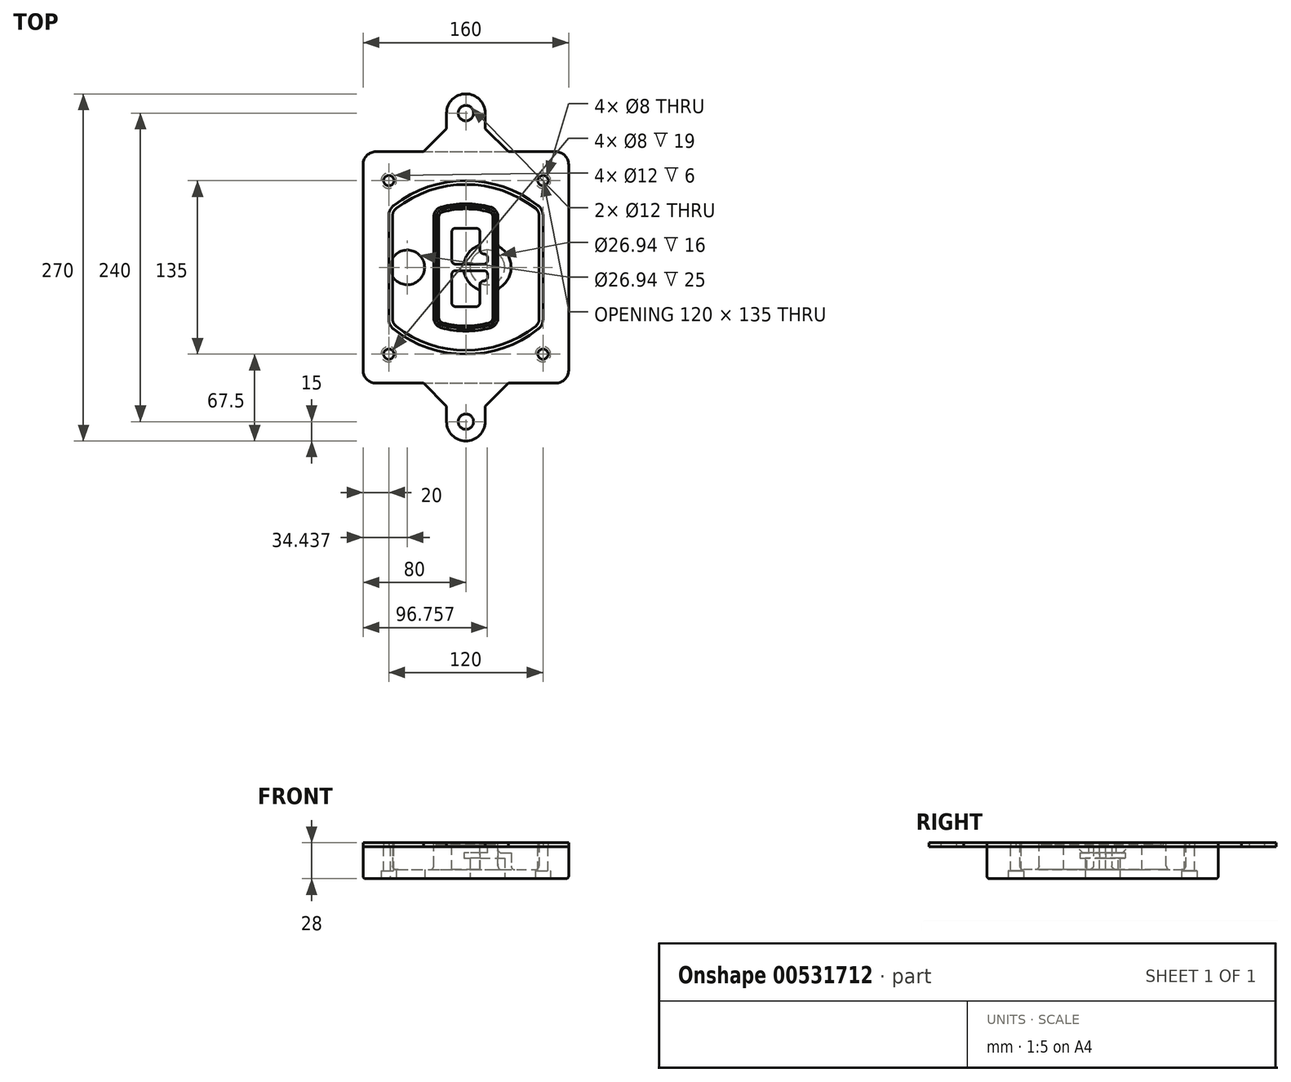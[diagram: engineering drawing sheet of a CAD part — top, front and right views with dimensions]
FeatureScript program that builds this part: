
annotation { "Feature Type Name" : "Feature", "Feature Type Description" : "" }
export const myFeature = defineFeature(function(context is Context, id is Id, definition is map)
    precondition{}
    {
        {
            var Q0;
            Q0=qCreatedBy(makeId("Top.planeOp"),FACE);
            var sketch = newSketch(context, id + "F0", { "sketchPlane" : qUnion([Q0])});
            skPoint(sketch, "E0.rect.middle", {"position": v(0, 0) * mm});
            skLineSegment(sketch, "E1.bottom", {"start": v(-70, -90) * mm, "end": v(70, -90) * mm});
            skLineSegment(sketch, "E1.top", {"start": v(-70, 90) * mm, "end": v(70, 90) * mm});
            skLineSegment(sketch, "E1.left", {"start": v(-80, -80) * mm, "end": v(-80, 80) * mm});
            skLineSegment(sketch, "E1.right", {"start": v(80, -80) * mm, "end": v(80, 80) * mm});
            skLineSegment(sketch, "E2", {"start": v(-80, 90) * mm, "end": v(80, -90) * mm, "construction": true});
            skLineSegment(sketch, "E3", {"start": v(80, 90) * mm, "end": v(-80, -90) * mm, "construction": true});
            skCircle(sketch, "E4", {"center": v(-60, 67.5) * mm, "radius": 4 * mm});
            skCircle(sketch, "E5", {"center": v(60, 67.5) * mm, "radius": 4 * mm});
            skCircle(sketch, "E6", {"center": v(60, -67.5) * mm, "radius": 4 * mm});
            skCircle(sketch, "E7", {"center": v(-60, -67.5) * mm, "radius": 4 * mm});
            skLineSegment(sketch, "E8", {"start": v(-60, 67.5) * mm, "end": v(60, 67.5) * mm, "construction": true});
            skLineSegment(sketch, "E9", {"start": v(60, 67.5) * mm, "end": v(60, -67.5) * mm, "construction": true});
            skLineSegment(sketch, "E10", {"start": v(60, -67.5) * mm, "end": v(-60, -67.5) * mm, "construction": true});
            skLineSegment(sketch, "E11", {"start": v(-60, -67.5) * mm, "end": v(-60, 67.5) * mm, "construction": true});
            skLineSegment(sketch, "E12", {"start": v(-60, 40.3) * mm, "end": v(-60, -40.3) * mm});
            skLineSegment(sketch, "E13", {"start": v(60, 40.3) * mm, "end": v(60, -40.3) * mm});
            skArc(sketch, "E14", {"start": v(56.15, 48.18) * mm, "mid": v(0, 67.5) * mm, "end": v(-56.15, 48.18) * mm});
            skArc(sketch, "E15", {"start": v(-56.15, -48.18) * mm, "mid": v(0, -67.5) * mm, "end": v(56.15, -48.18) * mm});
            skLineSegment(sketch, "E16", {"start": v(-60, 0) * mm, "end": v(60, 0) * mm, "construction": true});
            skPoint(sketch, "E17.visualSharp", {"position": v(-60, -45) * mm});
            skArc(sketch, "E17.filletArc", {"start": v(-60, -40.3) * mm, "mid": v(-58.99, -44.68) * mm, "end": v(-56.15, -48.18) * mm});
            skPoint(sketch, "E18.visualSharp", {"position": v(-60, 45) * mm});
            skArc(sketch, "E18.filletArc", {"start": v(-56.15, 48.18) * mm, "mid": v(-58.99, 44.68) * mm, "end": v(-60, 40.3) * mm});
            skPoint(sketch, "E19.visualSharp", {"position": v(60, 45) * mm});
            skArc(sketch, "E19.filletArc", {"start": v(60, 40.3) * mm, "mid": v(58.99, 44.68) * mm, "end": v(56.15, 48.18) * mm});
            skPoint(sketch, "E20.visualSharp", {"position": v(60, -45) * mm});
            skArc(sketch, "E20.filletArc", {"start": v(56.15, -48.18) * mm, "mid": v(58.99, -44.68) * mm, "end": v(60, -40.3) * mm});
            skPoint(sketch, "E21.visualSharp", {"position": v(-80, 90) * mm});
            skArc(sketch, "E21.filletArc", {"start": v(-70, 90) * mm, "mid": v(-77.07, 87.07) * mm, "end": v(-80, 80) * mm});
            skPoint(sketch, "E22.visualSharp", {"position": v(80, 90) * mm});
            skArc(sketch, "E22.filletArc", {"start": v(80, 80) * mm, "mid": v(77.07, 87.07) * mm, "end": v(70, 90) * mm});
            skPoint(sketch, "E23.visualSharp", {"position": v(80, -90) * mm});
            skArc(sketch, "E23.filletArc", {"start": v(70, -90) * mm, "mid": v(77.07, -87.07) * mm, "end": v(80, -80) * mm});
            skPoint(sketch, "E24.visualSharp", {"position": v(-80, -90) * mm});
            skArc(sketch, "E24.filletArc", {"start": v(-80, -80) * mm, "mid": v(-77.07, -87.07) * mm, "end": v(-70, -90) * mm});
            skArc(sketch, "E25.0", {"start": v(57, 40.3) * mm, "mid": v(56.3, 43.36) * mm, "end": v(54.3, 45.81) * mm});
            skLineSegment(sketch, "E25.1", {"start": v(57, 40.3) * mm, "end": v(57, -40.3) * mm});
            skArc(sketch, "E25.2", {"start": v(54.3, -45.81) * mm, "mid": v(56.3, -43.36) * mm, "end": v(57, -40.3) * mm});
            skArc(sketch, "E25.3", {"start": v(-54.3, -45.81) * mm, "mid": v(0, -64.5) * mm, "end": v(54.3, -45.81) * mm});
            skArc(sketch, "E25.4", {"start": v(-57, -40.3) * mm, "mid": v(-56.3, -43.36) * mm, "end": v(-54.3, -45.81) * mm});
            skArc(sketch, "E25.5", {"start": v(54.3, 45.81) * mm, "mid": v(0, 64.5) * mm, "end": v(-54.3, 45.81) * mm});
            skLineSegment(sketch, "E25.6", {"start": v(-57, 40.3) * mm, "end": v(-57, -40.3) * mm});
            skArc(sketch, "E25.7", {"start": v(-54.3, 45.81) * mm, "mid": v(-56.3, 43.36) * mm, "end": v(-57, 40.3) * mm});
            skArc(sketch, "E26.0", {"start": v(-58.62, 51.33) * mm, "mid": v(-62.58, 46.43) * mm, "end": v(-64, 40.3) * mm});
            skArc(sketch, "E26.1", {"start": v(58.62, 51.33) * mm, "mid": v(0, 71.5) * mm, "end": v(-58.62, 51.33) * mm});
            skArc(sketch, "E26.2", {"start": v(64, 40.3) * mm, "mid": v(62.58, 46.43) * mm, "end": v(58.62, 51.33) * mm});
            skLineSegment(sketch, "E26.3", {"start": v(64, 40.3) * mm, "end": v(64, -40.3) * mm});
            skArc(sketch, "E26.4", {"start": v(58.62, -51.33) * mm, "mid": v(62.58, -46.43) * mm, "end": v(64, -40.3) * mm});
            skLineSegment(sketch, "E26.5", {"start": v(-64, 40.3) * mm, "end": v(-64, -40.3) * mm});
            skArc(sketch, "E26.6", {"start": v(-58.62, -51.33) * mm, "mid": v(0, -71.5) * mm, "end": v(58.62, -51.33) * mm});
            skArc(sketch, "E26.7", {"start": v(-64, -40.3) * mm, "mid": v(-62.58, -46.43) * mm, "end": v(-58.62, -51.33) * mm});
            skSolve(sketch);
        }
        {
            var Q0;
            Q0=makeQuery(id+"F0.imprint","IMPRINT",FACE,{"disambiguationData":[TD([[makeQuery(id+"F0.imprint","IMPRINT",EDGE,{"derivedFrom":sQuery(id+"F0.wireOp",EDGE,"E1.bottom")}),1.0]])]});
            var Q1;
            Q1=makeQuery(id+"F0.imprint","IMPRINT",FACE,{"disambiguationData":[TD([[makeQuery(id+"F0.imprint","IMPRINT",EDGE,{"derivedFrom":sQuery(id+"F0.wireOp",EDGE,"E12")}),1.0]])]});
            var Q2;
            Q2=makeQuery(id+"F0.imprint","IMPRINT",FACE,{"disambiguationData":[TD([[makeQuery(id+"F0.imprint","IMPRINT",EDGE,{"derivedFrom":sQuery(id+"F0.wireOp",EDGE,"E25.0")}),1.0]])]});
            var Q3;
            Q3=makeQuery(id+"F0.imprint","IMPRINT",FACE,{"disambiguationData":[TD([[makeQuery(id+"F0.imprint","IMPRINT",EDGE,{"derivedFrom":sQuery(id+"F0.wireOp",EDGE,"E12")}),-1.0]])]});
            extrude(context, id + "F1", {"entities" : qUnion([Q0, Q1, Q2, Q3]), "oppositeDirection" : true, "depth" : 25 * mm});
        }
        {
            var Q0;
            Q0=makeQuery(id+"F0.imprint","IMPRINT",FACE,{"disambiguationData":[TD([[makeQuery(id+"F0.imprint","IMPRINT",EDGE,{"derivedFrom":sQuery(id+"F0.wireOp",EDGE,"E12")}),1.0]])]});
            extrude(context, id + "F2", {"entities" : qUnion([Q0]), "operationType" : NewBodyOperationType.ADD, "depth" : 3 * mm});
        }
        {
            var Q0;
            Q0=makeQuery(id+"F0.imprint","IMPRINT",FACE,{"disambiguationData":[TD([[makeQuery(id+"F0.imprint","IMPRINT",EDGE,{"derivedFrom":sQuery(id+"F0.wireOp",EDGE,"E25.0")}),1.0]])]});
            extrude(context, id + "F3", {"entities" : qUnion([Q0]), "operationType" : NewBodyOperationType.REMOVE, "oppositeDirection" : true, "depth" : 18 * mm});
        }
        {
            var Q0;
            Q0=makeQuery(id+"F2.opExtrude","CAP_FACE",FACE,{"disambiguationData":[OSD([sQuery(id+"F0.wireOp",EDGE,"E12"),sQuery(id+"F0.wireOp",EDGE,"E13"),sQuery(id+"F0.wireOp",EDGE,"E14"),sQuery(id+"F0.wireOp",EDGE,"E15"),sQuery(id+"F0.wireOp",EDGE,"E17.filletArc"),sQuery(id+"F0.wireOp",EDGE,"E18.filletArc"),sQuery(id+"F0.wireOp",EDGE,"E19.filletArc"),sQuery(id+"F0.wireOp",EDGE,"E20.filletArc"),sQuery(id+"F0.wireOp",EDGE,"E25.0"),sQuery(id+"F0.wireOp",EDGE,"E25.1"),sQuery(id+"F0.wireOp",EDGE,"E25.2"),sQuery(id+"F0.wireOp",EDGE,"E25.3"),sQuery(id+"F0.wireOp",EDGE,"E25.4"),sQuery(id+"F0.wireOp",EDGE,"E25.5"),sQuery(id+"F0.wireOp",EDGE,"E25.6"),sQuery(id+"F0.wireOp",EDGE,"E25.7")])],"isStart":false});
            var sketch = newSketch(context, id + "F4", { "sketchPlane" : qUnion([Q0])});
            skArc(sketch, "E27.0", {"start": v(-19.08, -46.97) * mm, "mid": v(0, -49.5) * mm, "end": v(19.08, -46.97) * mm});
            skArc(sketch, "E28.0", {"start": v(19.08, 46.97) * mm, "mid": v(0, 49.5) * mm, "end": v(-19.08, 46.97) * mm});
            skLineSegment(sketch, "E29", {"start": v(-25, 39.25) * mm, "end": v(-25, -39.25) * mm});
            skLineSegment(sketch, "E30", {"start": v(25, 39.25) * mm, "end": v(25, -39.25) * mm});
            skLineSegment(sketch, "E31", {"start": v(-25, 45.1) * mm, "end": v(25, 45.1) * mm, "construction": true});
            skLineSegment(sketch, "E32", {"start": v(-25, -45.1) * mm, "end": v(25, -45.1) * mm, "construction": true});
            skPoint(sketch, "E33.visualSharp", {"position": v(-25, 45.1) * mm});
            skArc(sketch, "E33.filletArc", {"start": v(-19.08, 46.97) * mm, "mid": v(-23.35, 44.11) * mm, "end": v(-25, 39.25) * mm});
            skPoint(sketch, "E34.visualSharp", {"position": v(25, 45.1) * mm});
            skArc(sketch, "E34.filletArc", {"start": v(25, 39.25) * mm, "mid": v(23.35, 44.11) * mm, "end": v(19.08, 46.97) * mm});
            skPoint(sketch, "E35.visualSharp", {"position": v(25, -45.1) * mm});
            skArc(sketch, "E35.filletArc", {"start": v(19.08, -46.97) * mm, "mid": v(23.35, -44.11) * mm, "end": v(25, -39.25) * mm});
            skPoint(sketch, "E36.visualSharp", {"position": v(-25, -45.1) * mm});
            skArc(sketch, "E36.filletArc", {"start": v(-25, -39.25) * mm, "mid": v(-23.35, -44.11) * mm, "end": v(-19.08, -46.97) * mm});
            skArc(sketch, "E37.0", {"start": v(54.3, 45.81) * mm, "mid": v(0, 64.5) * mm, "end": v(-54.3, 45.81) * mm});
            skArc(sketch, "E37.1", {"start": v(-54.3, 45.81) * mm, "mid": v(-56.3, 43.36) * mm, "end": v(-57, 40.3) * mm});
            skLineSegment(sketch, "E37.2", {"start": v(-57, 40.3) * mm, "end": v(-57, -40.3) * mm});
            skArc(sketch, "E37.3", {"start": v(-57, -40.3) * mm, "mid": v(-56.3, -43.36) * mm, "end": v(-54.3, -45.81) * mm});
            skArc(sketch, "E37.4", {"start": v(-54.3, -45.81) * mm, "mid": v(0, -64.5) * mm, "end": v(54.3, -45.81) * mm});
            skArc(sketch, "E37.5", {"start": v(54.3, -45.81) * mm, "mid": v(56.3, -43.36) * mm, "end": v(57, -40.3) * mm});
            skLineSegment(sketch, "E37.6", {"start": v(57, 40.3) * mm, "end": v(57, -40.3) * mm});
            skArc(sketch, "E37.7", {"start": v(57, 40.3) * mm, "mid": v(56.3, 43.36) * mm, "end": v(54.3, 45.81) * mm});
            skLineSegment(sketch, "E38.0", {"start": v(23, 39.25) * mm, "end": v(23, -39.25) * mm});
            skArc(sketch, "E38.1", {"start": v(18.56, -45.04) * mm, "mid": v(21.76, -42.9) * mm, "end": v(23, -39.25) * mm});
            skArc(sketch, "E38.2", {"start": v(-18.56, -45.04) * mm, "mid": v(0, -47.5) * mm, "end": v(18.56, -45.04) * mm});
            skArc(sketch, "E38.3", {"start": v(-23, -39.25) * mm, "mid": v(-21.76, -42.9) * mm, "end": v(-18.56, -45.04) * mm});
            skLineSegment(sketch, "E38.4", {"start": v(-23, 39.25) * mm, "end": v(-23, -39.25) * mm});
            skArc(sketch, "E38.5", {"start": v(23, 39.25) * mm, "mid": v(21.76, 42.9) * mm, "end": v(18.56, 45.04) * mm});
            skArc(sketch, "E38.6", {"start": v(-18.56, 45.04) * mm, "mid": v(-21.76, 42.9) * mm, "end": v(-23, 39.25) * mm});
            skArc(sketch, "E38.7", {"start": v(18.56, 45.04) * mm, "mid": v(0, 47.5) * mm, "end": v(-18.56, 45.04) * mm});
            skArc(sketch, "E39.0", {"start": v(21, 39.25) * mm, "mid": v(20.18, 41.68) * mm, "end": v(18.04, 43.1) * mm});
            skLineSegment(sketch, "E39.1", {"start": v(21, 39.25) * mm, "end": v(21, -39.25) * mm});
            skArc(sketch, "E39.2", {"start": v(18.04, -43.1) * mm, "mid": v(20.18, -41.68) * mm, "end": v(21, -39.25) * mm});
            skArc(sketch, "E39.3", {"start": v(-18.04, -43.1) * mm, "mid": v(0, -45.5) * mm, "end": v(18.04, -43.1) * mm});
            skArc(sketch, "E39.4", {"start": v(-21, -39.25) * mm, "mid": v(-20.18, -41.68) * mm, "end": v(-18.04, -43.1) * mm});
            skArc(sketch, "E39.5", {"start": v(18.04, 43.1) * mm, "mid": v(0, 45.5) * mm, "end": v(-18.04, 43.1) * mm});
            skLineSegment(sketch, "E39.6", {"start": v(-21, 39.25) * mm, "end": v(-21, -39.25) * mm});
            skArc(sketch, "E39.7", {"start": v(-18.04, 43.1) * mm, "mid": v(-20.18, 41.68) * mm, "end": v(-21, 39.25) * mm});
            skLineSegment(sketch, "E40", {"start": v(-25, 0) * mm, "end": v(25, 0) * mm, "construction": true});
            skLineSegment(sketch, "E41", {"start": v(-11, 5.5) * mm, "end": v(-11, 27.5) * mm});
            skLineSegment(sketch, "E42", {"start": v(-8, 30.5) * mm, "end": v(8, 30.5) * mm});
            skLineSegment(sketch, "E43", {"start": v(11, 27.5) * mm, "end": v(11, 13.5) * mm});
            skLineSegment(sketch, "E44", {"start": v(14, 10.5) * mm, "end": v(14, 10.5) * mm});
            skLineSegment(sketch, "E45", {"start": v(17, 7.5) * mm, "end": v(17, 5.5) * mm});
            skLineSegment(sketch, "E46", {"start": v(14, 2.5) * mm, "end": v(-8, 2.5) * mm});
            skPoint(sketch, "E47.visualSharp", {"position": v(-11, 30.5) * mm});
            skArc(sketch, "E47.filletArc", {"start": v(-8, 30.5) * mm, "mid": v(-10.12, 29.62) * mm, "end": v(-11, 27.5) * mm});
            skPoint(sketch, "E48.visualSharp", {"position": v(11, 30.5) * mm});
            skArc(sketch, "E48.filletArc", {"start": v(11, 27.5) * mm, "mid": v(10.12, 29.62) * mm, "end": v(8, 30.5) * mm});
            skPoint(sketch, "E49.visualSharp", {"position": v(11, 10.5) * mm});
            skArc(sketch, "E49.filletArc", {"start": v(11, 13.5) * mm, "mid": v(11.88, 11.38) * mm, "end": v(14, 10.5) * mm});
            skPoint(sketch, "E50.visualSharp", {"position": v(17, 10.5) * mm});
            skArc(sketch, "E50.filletArc", {"start": v(17, 7.5) * mm, "mid": v(16.12, 9.62) * mm, "end": v(14, 10.5) * mm});
            skPoint(sketch, "E51.visualSharp", {"position": v(17, 2.5) * mm});
            skArc(sketch, "E51.filletArc", {"start": v(14, 2.5) * mm, "mid": v(16.12, 3.38) * mm, "end": v(17, 5.5) * mm});
            skPoint(sketch, "E52.visualSharp", {"position": v(-11, 2.5) * mm});
            skArc(sketch, "E52.filletArc", {"start": v(-11, 5.5) * mm, "mid": v(-10.12, 3.38) * mm, "end": v(-8, 2.5) * mm});
            skLineSegment(sketch, "E53.0.MirrorCS", {"start": v(14, -2.5) * mm, "end": v(-8, -2.5) * mm});
            skArc(sketch, "E54.0.MirrorCS", {"start": v(-11, -5.5) * mm, "mid": v(-10.12, -3.38) * mm, "end": v(-8, -2.5) * mm});
            skLineSegment(sketch, "E55.0.MirrorCS", {"start": v(-11, -5.5) * mm, "end": v(-11, -27.5) * mm});
            skArc(sketch, "E56.0.MirrorCS", {"start": v(-8, -30.5) * mm, "mid": v(-10.12, -29.62) * mm, "end": v(-11, -27.5) * mm});
            skLineSegment(sketch, "E57.0.MirrorCS", {"start": v(-8, -30.5) * mm, "end": v(8, -30.5) * mm});
            skArc(sketch, "E58.0.MirrorCS", {"start": v(11, -27.5) * mm, "mid": v(10.12, -29.62) * mm, "end": v(8, -30.5) * mm});
            skLineSegment(sketch, "E59.0.MirrorCS", {"start": v(11, -27.5) * mm, "end": v(11, -13.5) * mm});
            skArc(sketch, "E60.0.MirrorCS", {"start": v(11, -13.5) * mm, "mid": v(11.88, -11.38) * mm, "end": v(14, -10.5) * mm});
            skArc(sketch, "E61.0.MirrorCS", {"start": v(17, -7.5) * mm, "mid": v(16.12, -9.62) * mm, "end": v(14, -10.5) * mm});
            skLineSegment(sketch, "E62.0.MirrorCS", {"start": v(17, -7.5) * mm, "end": v(17, -5.5) * mm});
            skArc(sketch, "E63.0.MirrorCS", {"start": v(14, -2.5) * mm, "mid": v(16.12, -3.38) * mm, "end": v(17, -5.5) * mm});
            skSolve(sketch);
        }
        {
            var Q0;
            Q0=makeQuery(id+"F4.imprint","IMPRINT",FACE,{"disambiguationData":[TD([[makeQuery(id+"F4.imprint","IMPRINT",EDGE,{"derivedFrom":sQuery(id+"F4.wireOp",EDGE,"E27.0")}),1.0]])]});
            var Q1;
            Q1=makeQuery(id+"F4.imprint","IMPRINT",FACE,{"disambiguationData":[TD([[makeQuery(id+"F4.imprint","IMPRINT",EDGE,{"derivedFrom":sQuery(id+"F4.wireOp",EDGE,"E38.0")}),-1.0]])]});
            var Q2;
            Q2=makeQuery(id+"F4.imprint","IMPRINT",FACE,{"disambiguationData":[TD([[makeQuery(id+"F4.imprint","IMPRINT",EDGE,{"derivedFrom":sQuery(id+"F4.wireOp",EDGE,"E39.0")}),1.0]])]});
            extrude(context, id + "F5", {"entities" : qUnion([Q0, Q1, Q2]), "operationType" : NewBodyOperationType.ADD, "endBound" : BoundingType.UP_TO_NEXT, "oppositeDirection" : true, "depth" : 25 * mm});
        }
        {
            var Q0;
            Q0=makeQuery(id+"F4.imprint","IMPRINT",FACE,{"disambiguationData":[TD([[makeQuery(id+"F4.imprint","IMPRINT",EDGE,{"derivedFrom":sQuery(id+"F4.wireOp",EDGE,"E38.0")}),-1.0]])]});
            extrude(context, id + "F6", {"entities" : qUnion([Q0]), "operationType" : NewBodyOperationType.REMOVE, "oppositeDirection" : true, "depth" : 2 * mm});
        }
        {
            var Q0;
            Q0=makeQuery(id+"F1.opExtrude","CAP_FACE",FACE,{"disambiguationData":[OSD([sQuery(id+"F0.wireOp",EDGE,"E1.bottom"),sQuery(id+"F0.wireOp",EDGE,"E1.top"),sQuery(id+"F0.wireOp",EDGE,"E1.left"),sQuery(id+"F0.wireOp",EDGE,"E1.right"),sQuery(id+"F0.wireOp",EDGE,"E4"),sQuery(id+"F0.wireOp",EDGE,"E5"),sQuery(id+"F0.wireOp",EDGE,"E6"),sQuery(id+"F0.wireOp",EDGE,"E7"),sQuery(id+"F0.wireOp",EDGE,"E21.filletArc"),sQuery(id+"F0.wireOp",EDGE,"E22.filletArc"),sQuery(id+"F0.wireOp",EDGE,"E23.filletArc"),sQuery(id+"F0.wireOp",EDGE,"E24.filletArc")])],"isStart":false});
            var sketch = newSketch(context, id + "F7", { "sketchPlane" : qUnion([Q0])});
            skCircle(sketch, "E64", {"center": v(16.76, 0) * mm, "radius": 13.47 * mm});
            skCircle(sketch, "E65", {"center": v(-45.56, 0) * mm, "radius": 13.47 * mm});
            skLineSegment(sketch, "E66", {"start": v(80, 0) * mm, "end": v(-80, 0) * mm});
            skCircle(sketch, "E67", {"center": v(16.76, 0) * mm, "radius": 18.47 * mm});
            skCircle(sketch, "E68", {"center": v(60, -67.5) * mm, "radius": 6 * mm});
            skCircle(sketch, "E69", {"center": v(-60, -67.5) * mm, "radius": 6 * mm});
            skCircle(sketch, "E70", {"center": v(-60, 67.5) * mm, "radius": 6 * mm});
            skCircle(sketch, "E71", {"center": v(60, 67.5) * mm, "radius": 6 * mm});
            skSolve(sketch);
        }
        {
            var Q0;
            {var subQ1=sQuery(id+"F7.wireOp",EDGE,"E66");var subQ4=sQuery(id+"F7.wireOp",EDGE,"E64");var subQ6=makeQuery(id+"F7.imprint","INTERSECT",VERTEX,{"disambiguationData":[OD(0.0)],"derivedFrom":[subQ4,subQ1]});Q0=makeQuery(id+"F7.imprint","IMPRINT",FACE,{"disambiguationData":[TD([[makeQuery(id+"F7.imprint","IMPRINT",EDGE,{"disambiguationData":[TD([[subQ6,-1.0]])],"derivedFrom":subQ4}),-1.0]])]});}
            var Q1;
            {var subQ0=sQuery(id+"F7.wireOp",EDGE,"E66");var subQ1=sQuery(id+"F7.wireOp",EDGE,"E64");var subQ3=makeQuery(id+"F7.imprint","INTERSECT",VERTEX,{"disambiguationData":[OD(0.0)],"derivedFrom":[subQ1,subQ0]});Q1=makeQuery(id+"F7.imprint","IMPRINT",FACE,{"disambiguationData":[TD([[makeQuery(id+"F7.imprint","IMPRINT",EDGE,{"disambiguationData":[TD([[subQ3,-1.0]])],"derivedFrom":subQ1}),1.0]])]});}
            var Q2;
            {var subQ0=sQuery(id+"F7.wireOp",EDGE,"E66");var subQ1=sQuery(id+"F7.wireOp",EDGE,"E64");var subQ3=makeQuery(id+"F7.imprint","INTERSECT",VERTEX,{"disambiguationData":[OD(0.0)],"derivedFrom":[subQ1,subQ0]});Q2=makeQuery(id+"F7.imprint","IMPRINT",FACE,{"disambiguationData":[TD([[makeQuery(id+"F7.imprint","IMPRINT",EDGE,{"disambiguationData":[TD([[subQ3,1.0]])],"derivedFrom":subQ1}),1.0]])]});}
            var Q3;
            {var subQ1=sQuery(id+"F7.wireOp",EDGE,"E66");var subQ4=sQuery(id+"F7.wireOp",EDGE,"E64");var subQ6=makeQuery(id+"F7.imprint","INTERSECT",VERTEX,{"disambiguationData":[OD(0.0)],"derivedFrom":[subQ4,subQ1]});Q3=makeQuery(id+"F7.imprint","IMPRINT",FACE,{"disambiguationData":[TD([[makeQuery(id+"F7.imprint","IMPRINT",EDGE,{"disambiguationData":[TD([[subQ6,1.0]])],"derivedFrom":subQ4}),-1.0]])]});}
            extrude(context, id + "F8", {"entities" : qUnion([Q0, Q1, Q2, Q3]), "operationType" : NewBodyOperationType.ADD, "oppositeDirection" : true, "depth" : 20 * mm});
        }
        {
            var Q0;
            {var subQ0=sQuery(id+"F7.wireOp",EDGE,"E66");var subQ1=sQuery(id+"F7.wireOp",EDGE,"E64");var subQ3=makeQuery(id+"F7.imprint","INTERSECT",VERTEX,{"disambiguationData":[OD(0.0)],"derivedFrom":[subQ1,subQ0]});Q0=makeQuery(id+"F7.imprint","IMPRINT",FACE,{"disambiguationData":[TD([[makeQuery(id+"F7.imprint","IMPRINT",EDGE,{"disambiguationData":[TD([[subQ3,-1.0]])],"derivedFrom":subQ1}),1.0]])]});}
            var Q1;
            {var subQ0=sQuery(id+"F7.wireOp",EDGE,"E66");var subQ1=sQuery(id+"F7.wireOp",EDGE,"E64");var subQ3=makeQuery(id+"F7.imprint","INTERSECT",VERTEX,{"disambiguationData":[OD(0.0)],"derivedFrom":[subQ1,subQ0]});Q1=makeQuery(id+"F7.imprint","IMPRINT",FACE,{"disambiguationData":[TD([[makeQuery(id+"F7.imprint","IMPRINT",EDGE,{"disambiguationData":[TD([[subQ3,1.0]])],"derivedFrom":subQ1}),1.0]])]});}
            extrude(context, id + "F9", {"entities" : qUnion([Q0, Q1]), "operationType" : NewBodyOperationType.REMOVE, "oppositeDirection" : true, "depth" : 16 * mm});
        }
        {
            var Q0;
            {var subQ0=sQuery(id+"F7.wireOp",EDGE,"E66");var subQ1=sQuery(id+"F7.wireOp",EDGE,"E65");var subQ3=makeQuery(id+"F7.imprint","INTERSECT",VERTEX,{"disambiguationData":[OD(0.0)],"derivedFrom":[subQ1,subQ0]});Q0=makeQuery(id+"F7.imprint","IMPRINT",FACE,{"disambiguationData":[TD([[makeQuery(id+"F7.imprint","IMPRINT",EDGE,{"disambiguationData":[TD([[subQ3,-1.0]])],"derivedFrom":subQ1}),1.0]])]});}
            var Q1;
            {var subQ0=sQuery(id+"F7.wireOp",EDGE,"E66");var subQ1=sQuery(id+"F7.wireOp",EDGE,"E65");var subQ3=makeQuery(id+"F7.imprint","INTERSECT",VERTEX,{"disambiguationData":[OD(0.0)],"derivedFrom":[subQ1,subQ0]});Q1=makeQuery(id+"F7.imprint","IMPRINT",FACE,{"disambiguationData":[TD([[makeQuery(id+"F7.imprint","IMPRINT",EDGE,{"disambiguationData":[TD([[subQ3,1.0]])],"derivedFrom":subQ1}),1.0]])]});}
            extrude(context, id + "F10", {"entities" : qUnion([Q0, Q1]), "operationType" : NewBodyOperationType.REMOVE, "oppositeDirection" : true, "depth" : 25 * mm});
        }
        {
            var Q0;
            Q0=makeQuery(id+"F7.imprint","IMPRINT",FACE,{"disambiguationData":[TD([[makeQuery(id+"F7.imprint","IMPRINT",EDGE,{"derivedFrom":sQuery(id+"F7.wireOp",EDGE,"E68")}),1.0]])]});
            var Q1;
            Q1=makeQuery(id+"F7.imprint","IMPRINT",FACE,{"disambiguationData":[TD([[makeQuery(id+"F7.imprint","IMPRINT",EDGE,{"derivedFrom":makeQuery(id+"F1.opExtrude","CAP_EDGE",EDGE,{"disambiguationData":[OSD([sQuery(id+"F0.wireOp",EDGE,"E5")])],"isStart":false})}),-1.0]])]});
            var Q2;
            Q2=makeQuery(id+"F7.imprint","IMPRINT",FACE,{"disambiguationData":[TD([[makeQuery(id+"F7.imprint","IMPRINT",EDGE,{"derivedFrom":sQuery(id+"F7.wireOp",EDGE,"E69")}),1.0]])]});
            var Q3;
            Q3=makeQuery(id+"F7.imprint","IMPRINT",FACE,{"disambiguationData":[TD([[makeQuery(id+"F7.imprint","IMPRINT",EDGE,{"derivedFrom":makeQuery(id+"F1.opExtrude","CAP_EDGE",EDGE,{"disambiguationData":[OSD([sQuery(id+"F0.wireOp",EDGE,"E4")])],"isStart":false})}),-1.0]])]});
            var Q4;
            Q4=makeQuery(id+"F7.imprint","IMPRINT",FACE,{"disambiguationData":[TD([[makeQuery(id+"F7.imprint","IMPRINT",EDGE,{"derivedFrom":sQuery(id+"F7.wireOp",EDGE,"E70")}),1.0]])]});
            var Q5;
            Q5=makeQuery(id+"F7.imprint","IMPRINT",FACE,{"disambiguationData":[TD([[makeQuery(id+"F7.imprint","IMPRINT",EDGE,{"derivedFrom":makeQuery(id+"F1.opExtrude","CAP_EDGE",EDGE,{"disambiguationData":[OSD([sQuery(id+"F0.wireOp",EDGE,"E7")])],"isStart":false})}),-1.0]])]});
            var Q6;
            Q6=makeQuery(id+"F7.imprint","IMPRINT",FACE,{"disambiguationData":[TD([[makeQuery(id+"F7.imprint","IMPRINT",EDGE,{"derivedFrom":sQuery(id+"F7.wireOp",EDGE,"E71")}),1.0]])]});
            var Q7;
            Q7=makeQuery(id+"F7.imprint","IMPRINT",FACE,{"disambiguationData":[TD([[makeQuery(id+"F7.imprint","IMPRINT",EDGE,{"derivedFrom":makeQuery(id+"F1.opExtrude","CAP_EDGE",EDGE,{"disambiguationData":[OSD([sQuery(id+"F0.wireOp",EDGE,"E6")])],"isStart":false})}),-1.0]])]});
            extrude(context, id + "F11", {"entities" : qUnion([Q0, Q1, Q2, Q3, Q4, Q5, Q6, Q7]), "operationType" : NewBodyOperationType.REMOVE, "oppositeDirection" : true, "depth" : 6 * mm});
        }
        {
            var Q0;
            Q0=makeQuery(id+"F9.boolean.opBoolean","COPY",FACE,{"derivedFrom":makeQuery(id+"F9.opExtrude","CAP_FACE",FACE,{"disambiguationData":[OSD([sQuery(id+"F7.wireOp",EDGE,"E64")])],"isStart":false})});
            var sketch = newSketch(context, id + "F12", { "sketchPlane" : qUnion([Q0])});
            skArc(sketch, "E72.0", {"start": v(11, 17.55) * mm, "mid": v(2.57, 11.82) * mm, "end": v(-1.54, 2.5) * mm});
            skArc(sketch, "E72.1", {"start": v(-1.54, -2.5) * mm, "mid": v(2.57, -11.82) * mm, "end": v(11, -17.55) * mm});
            skLineSegment(sketch, "E73", {"start": v(-1.54, -2.5) * mm, "end": v(14, -2.5) * mm});
            skLineSegment(sketch, "E74.0", {"start": v(14, 2.5) * mm, "end": v(-1.54, 2.5) * mm});
            skArc(sketch, "E74.1", {"start": v(14, 2.5) * mm, "mid": v(16.12, 3.38) * mm, "end": v(17, 5.5) * mm});
            skLineSegment(sketch, "E74.2", {"start": v(17, 7.5) * mm, "end": v(17, 5.5) * mm});
            skArc(sketch, "E74.3", {"start": v(17, 7.5) * mm, "mid": v(16.12, 9.62) * mm, "end": v(14, 10.5) * mm});
            skArc(sketch, "E74.4", {"start": v(11, 13.5) * mm, "mid": v(11.88, 11.38) * mm, "end": v(14, 10.5) * mm});
            skLineSegment(sketch, "E74.5", {"start": v(11, 17.55) * mm, "end": v(11, 13.5) * mm});
            skLineSegment(sketch, "E74.7", {"start": v(14, -2.5) * mm, "end": v(-1.54, -2.5) * mm});
            skArc(sketch, "E74.8", {"start": v(14, -2.5) * mm, "mid": v(16.12, -3.38) * mm, "end": v(17, -5.5) * mm});
            skLineSegment(sketch, "E74.9", {"start": v(17, -7.5) * mm, "end": v(17, -5.5) * mm});
            skArc(sketch, "E74.10", {"start": v(17, -7.5) * mm, "mid": v(16.12, -9.62) * mm, "end": v(14, -10.5) * mm});
            skArc(sketch, "E74.11", {"start": v(11, -13.5) * mm, "mid": v(11.88, -11.38) * mm, "end": v(14, -10.5) * mm});
            skLineSegment(sketch, "E74.12", {"start": v(11, -17.55) * mm, "end": v(11, -13.5) * mm});
            skPoint(sketch, "E75.orphan", {"position": v(11, -27.5) * mm});
            skPoint(sketch, "E76.orphan", {"position": v(-8, -2.5) * mm});
            skPoint(sketch, "E77.orphan", {"position": v(-8, 2.5) * mm});
            skPoint(sketch, "E78.orphan", {"position": v(11, 27.5) * mm});
            skSolve(sketch);
        }
        {
            var Q0;
            {var subQ7=sQuery(id+"F12.wireOp",EDGE,"E72.0");var subQ14=sQuery(id+"F12.wireOp",EDGE,"E72.1");var subQ16=sQuery(id+"F12.wireOp",EDGE,"E74.1");var subQ18=sQuery(id+"F12.wireOp",EDGE,"E74.8");Q0=qUnion([makeQuery(id+"F12.imprint","IMPRINT",FACE,{"disambiguationData":[TD([[makeQuery(id+"F12.imprint","IMPRINT",EDGE,{"derivedFrom":subQ7}),1.0]])]}),makeQuery(id+"F12.imprint","IMPRINT",FACE,{"disambiguationData":[TD([[makeQuery(id+"F12.imprint","IMPRINT",EDGE,{"derivedFrom":subQ14}),1.0]])]}),makeQuery(id+"F12.imprint","IMPRINT",FACE,{"disambiguationData":[TD([[makeQuery(id+"F12.imprint","IMPRINT",EDGE,{"derivedFrom":subQ16}),1.0]])]}),makeQuery(id+"F12.imprint","IMPRINT",FACE,{"disambiguationData":[TD([[makeQuery(id+"F12.imprint","IMPRINT",EDGE,{"derivedFrom":subQ18}),-1.0]])]})]);}
            var Q1;
            Q1=makeQuery(id+"F5.boolean.opBoolean","SPLIT",FACE,{"disambiguationData":[TD([makeQuery(id+"F5.opExtrude","SWEPT_FACE",FACE,{"disambiguationData":[OSD([sQuery(id+"F4.wireOp",EDGE,"E41")])]})])],"derivedFrom":makeQuery(id+"F3.boolean.opBoolean","COPY",FACE,{"derivedFrom":makeQuery(id+"F3.opExtrude","CAP_FACE",FACE,{"disambiguationData":[OSD([sQuery(id+"F0.wireOp",EDGE,"E25.0"),sQuery(id+"F0.wireOp",EDGE,"E25.1"),sQuery(id+"F0.wireOp",EDGE,"E25.2"),sQuery(id+"F0.wireOp",EDGE,"E25.3"),sQuery(id+"F0.wireOp",EDGE,"E25.4"),sQuery(id+"F0.wireOp",EDGE,"E25.5"),sQuery(id+"F0.wireOp",EDGE,"E25.6"),sQuery(id+"F0.wireOp",EDGE,"E25.7")])],"isStart":false})})});
            extrude(context, id + "F13", {"entities" : qUnion([Q0]), "operationType" : NewBodyOperationType.REMOVE, "endBound" : BoundingType.UP_TO_SURFACE, "endBoundEntityFace" : qUnion([Q1]), "depth" : 25 * mm});
        }
        {
            var Q0;
            Q0=makeQuery(id+"F3.boolean.opBoolean","COPY",EDGE,{"derivedFrom":makeQuery(id+"F3.opExtrude","CAP_EDGE",EDGE,{"disambiguationData":[OSD([sQuery(id+"F0.wireOp",EDGE,"E25.6")])],"isStart":false})});
            var Q1;
            Q1=makeQuery(id+"F8.boolean.opBoolean","INTERSECT",EDGE,{"derivedFrom":[makeQuery(id+"F5.opExtrude","SWEPT_FACE",FACE,{"disambiguationData":[OSD([sQuery(id+"F4.wireOp",EDGE,"E30")])]}),makeQuery(id+"F8.opExtrude","CAP_FACE",FACE,{"disambiguationData":[OSD([sQuery(id+"F7.wireOp",EDGE,"E67")])],"isStart":false})]});
            var Q2;
            Q2=makeQuery(id+"F8.boolean.opBoolean","INTERSECT",EDGE,{"disambiguationData":[OD(1.0)],"derivedFrom":[makeQuery(id+"F5.opExtrude","SWEPT_FACE",FACE,{"disambiguationData":[OSD([sQuery(id+"F4.wireOp",EDGE,"E30")])]}),makeQuery(id+"F8.opExtrude","SWEPT_FACE",FACE,{"disambiguationData":[OSD([sQuery(id+"F7.wireOp",EDGE,"E67")])]})]});
            var Q3;
            {var subQ0=sQuery(id+"F4.wireOp",EDGE,"E30");Q3=makeQuery(id+"F8.boolean.opBoolean","SPLIT",EDGE,{"disambiguationData":[TD([makeQuery(id+"F5.opExtrude","SWEPT_FACE",FACE,{"disambiguationData":[OSD([sQuery(id+"F4.wireOp",EDGE,"E35.filletArc")])]})])],"derivedFrom":makeQuery(id+"F5.opExtrude","CAP_EDGE",EDGE,{"disambiguationData":[OSD([subQ0])],"isStart":false})});}
            var Q4;
            {var subQ0=sQuery(id+"F0.wireOp",EDGE,"E25.7");var subQ1=sQuery(id+"F0.wireOp",EDGE,"E25.1");var subQ2=sQuery(id+"F0.wireOp",EDGE,"E25.6");var subQ3=sQuery(id+"F0.wireOp",EDGE,"E25.5");var subQ4=sQuery(id+"F0.wireOp",EDGE,"E25.4");var subQ5=sQuery(id+"F0.wireOp",EDGE,"E25.0");var subQ6=sQuery(id+"F0.wireOp",EDGE,"E25.2");var subQ7=sQuery(id+"F0.wireOp",EDGE,"E25.3");Q4=makeQuery(id+"F8.boolean.opBoolean","INTERSECT",EDGE,{"derivedFrom":[makeQuery(id+"F5.boolean.opBoolean","SPLIT",FACE,{"disambiguationData":[TD([makeQuery(id+"F2.opExtrude","SWEPT_FACE",FACE,{"disambiguationData":[OSD([subQ5])]})])],"derivedFrom":makeQuery(id+"F3.boolean.opBoolean","COPY",FACE,{"derivedFrom":makeQuery(id+"F3.opExtrude","CAP_FACE",FACE,{"disambiguationData":[OSD([subQ5,subQ1,subQ6,subQ7,subQ4,subQ3,subQ2,subQ0])],"isStart":false})})}),makeQuery(id+"F8.opExtrude","SWEPT_FACE",FACE,{"disambiguationData":[OSD([sQuery(id+"F7.wireOp",EDGE,"E67")])]})]});}
            var Q5;
            Q5=makeQuery(id+"F8.boolean.opBoolean","INTERSECT",EDGE,{"disambiguationData":[OD(0.0)],"derivedFrom":[makeQuery(id+"F5.opExtrude","SWEPT_FACE",FACE,{"disambiguationData":[OSD([sQuery(id+"F4.wireOp",EDGE,"E30")])]}),makeQuery(id+"F8.opExtrude","SWEPT_FACE",FACE,{"disambiguationData":[OSD([sQuery(id+"F7.wireOp",EDGE,"E67")])]})]});
            fillet(context, id + "F14", {"entities" : qUnion([Q0, Q1, Q2, Q3, Q4, Q5]), "radius" : 3 * mm, "tangentPropagation" : true, "allowEdgeOverflow" : false});
        }
        {
            var Q0;
            Q0=makeQuery(id+"F1.opExtrude","CAP_EDGE",EDGE,{"disambiguationData":[OSD([sQuery(id+"F0.wireOp",EDGE,"E1.bottom")])],"isStart":false});
            fillet(context, id + "F15", {"entities" : qUnion([Q0]), "radius" : 2 * mm, "tangentPropagation" : true, "allowEdgeOverflow" : false});
        }
        {
            var Q0;
            {var subQ0=sQuery(id+"F0.wireOp",EDGE,"E21.filletArc");var subQ1=sQuery(id+"F0.wireOp",EDGE,"E7");var subQ2=sQuery(id+"F0.wireOp",EDGE,"E6");var subQ3=sQuery(id+"F0.wireOp",EDGE,"E5");var subQ4=sQuery(id+"F0.wireOp",EDGE,"E4");var subQ5=sQuery(id+"F0.wireOp",EDGE,"E22.filletArc");var subQ6=sQuery(id+"F0.wireOp",EDGE,"E1.bottom");var subQ7=sQuery(id+"F0.wireOp",EDGE,"E1.right");var subQ8=sQuery(id+"F0.wireOp",EDGE,"E1.top");var subQ9=sQuery(id+"F0.wireOp",EDGE,"E1.left");var subQ10=sQuery(id+"F0.wireOp",EDGE,"E23.filletArc");var subQ11=sQuery(id+"F0.wireOp",EDGE,"E24.filletArc");Q0=makeQuery(id+"F2.boolean.opBoolean","SPLIT",FACE,{"disambiguationData":[TD([makeQuery(id+"F1.opExtrude","SWEPT_FACE",FACE,{"disambiguationData":[OSD([subQ6])]})])],"derivedFrom":makeQuery(id+"F1.opExtrude","CAP_FACE",FACE,{"disambiguationData":[OSD([subQ6,subQ8,subQ9,subQ7,subQ4,subQ3,subQ2,subQ1,subQ0,subQ5,subQ10,subQ11])],"isStart":true})});}
            var sketch = newSketch(context, id + "F16", { "sketchPlane" : qUnion([Q0])});
            skLineSegment(sketch, "E79", {"start": v(0, 90) * mm, "end": v(0, 90) * mm});
            skLineSegment(sketch, "E80", {"start": v(0, 90) * mm, "end": v(0, 120) * mm, "construction": true});
            skCircle(sketch, "E81", {"center": v(0, 120) * mm, "radius": 6 * mm});
            skArc(sketch, "E82", {"start": v(15, 120) * mm, "mid": v(0, 135) * mm, "end": v(-15, 120) * mm});
            skLineSegment(sketch, "E83", {"start": v(-15, 120) * mm, "end": v(-15, 108) * mm});
            skLineSegment(sketch, "E84", {"start": v(15, 120) * mm, "end": v(15, 108) * mm});
            skLineSegment(sketch, "E85", {"start": v(15, 108) * mm, "end": v(33, 90) * mm});
            skLineSegment(sketch, "E86.MirrorCS", {"start": v(-15, 108) * mm, "end": v(-33, 90) * mm});
            skLineSegment(sketch, "E87", {"start": v(-80, 0) * mm, "end": v(80, 0) * mm, "construction": true});
            skLineSegment(sketch, "E88.MirrorCS", {"start": v(-15, -120) * mm, "end": v(-15, -108) * mm});
            skLineSegment(sketch, "E89.MirrorCS", {"start": v(15, -120) * mm, "end": v(15, -108) * mm});
            skCircle(sketch, "E90.MirrorC", {"center": v(0, -120) * mm, "radius": 6 * mm});
            skArc(sketch, "E91.MirrorCS", {"start": v(15, -120) * mm, "mid": v(0, -135) * mm, "end": v(-15, -120) * mm});
            skLineSegment(sketch, "E92.MirrorCS", {"start": v(0, -90) * mm, "end": v(0, -90) * mm});
            skLineSegment(sketch, "E93.MirrorCS", {"start": v(15, -108) * mm, "end": v(33, -90) * mm});
            skLineSegment(sketch, "E94.MirrorCS", {"start": v(-15, -108) * mm, "end": v(-33, -90) * mm});
            skLineSegment(sketch, "E95.MirrorCS", {"start": v(0, -90) * mm, "end": v(0, -120) * mm, "construction": true});
            skSolve(sketch);
        }
        {
            var Q0;
            Q0=makeQuery(id+"F16.imprint","IMPRINT",FACE,{"disambiguationData":[TD([[makeQuery(id+"F16.imprint","IMPRINT",EDGE,{"derivedFrom":sQuery(id+"F16.wireOp",EDGE,"E81")}),-1.0]])]});
            var Q1;
            Q1=makeQuery(id+"F16.imprint","IMPRINT",FACE,{"disambiguationData":[TD([[makeQuery(id+"F16.imprint","IMPRINT",EDGE,{"derivedFrom":makeQuery(id+"F1.opExtrude","CAP_EDGE",EDGE,{"disambiguationData":[OSD([sQuery(id+"F0.wireOp",EDGE,"E1.left")])],"isStart":true})}),-1.0]])]});
            var Q2;
            Q2=makeQuery(id+"F16.imprint","IMPRINT",FACE,{"disambiguationData":[TD([[makeQuery(id+"F16.imprint","IMPRINT",EDGE,{"derivedFrom":sQuery(id+"F16.wireOp",EDGE,"E88.MirrorCS")}),-1.0]])]});
            var Q3;
            Q3=makeQuery(id+"F2.opExtrude","CAP_FACE",FACE,{"disambiguationData":[OSD([sQuery(id+"F0.wireOp",EDGE,"E12"),sQuery(id+"F0.wireOp",EDGE,"E13"),sQuery(id+"F0.wireOp",EDGE,"E14"),sQuery(id+"F0.wireOp",EDGE,"E15"),sQuery(id+"F0.wireOp",EDGE,"E17.filletArc"),sQuery(id+"F0.wireOp",EDGE,"E18.filletArc"),sQuery(id+"F0.wireOp",EDGE,"E19.filletArc"),sQuery(id+"F0.wireOp",EDGE,"E20.filletArc"),sQuery(id+"F0.wireOp",EDGE,"E25.0"),sQuery(id+"F0.wireOp",EDGE,"E25.1"),sQuery(id+"F0.wireOp",EDGE,"E25.2"),sQuery(id+"F0.wireOp",EDGE,"E25.3"),sQuery(id+"F0.wireOp",EDGE,"E25.4"),sQuery(id+"F0.wireOp",EDGE,"E25.5"),sQuery(id+"F0.wireOp",EDGE,"E25.6"),sQuery(id+"F0.wireOp",EDGE,"E25.7")])],"isStart":false});
            extrude(context, id + "F17", {"entities" : qUnion([Q0, Q1, Q2]), "endBound" : BoundingType.UP_TO_SURFACE, "depth" : 25 * mm, "endBoundEntityFace" : qUnion([Q3]), "offsetDistance" : 25 * mm});
        }
    });
